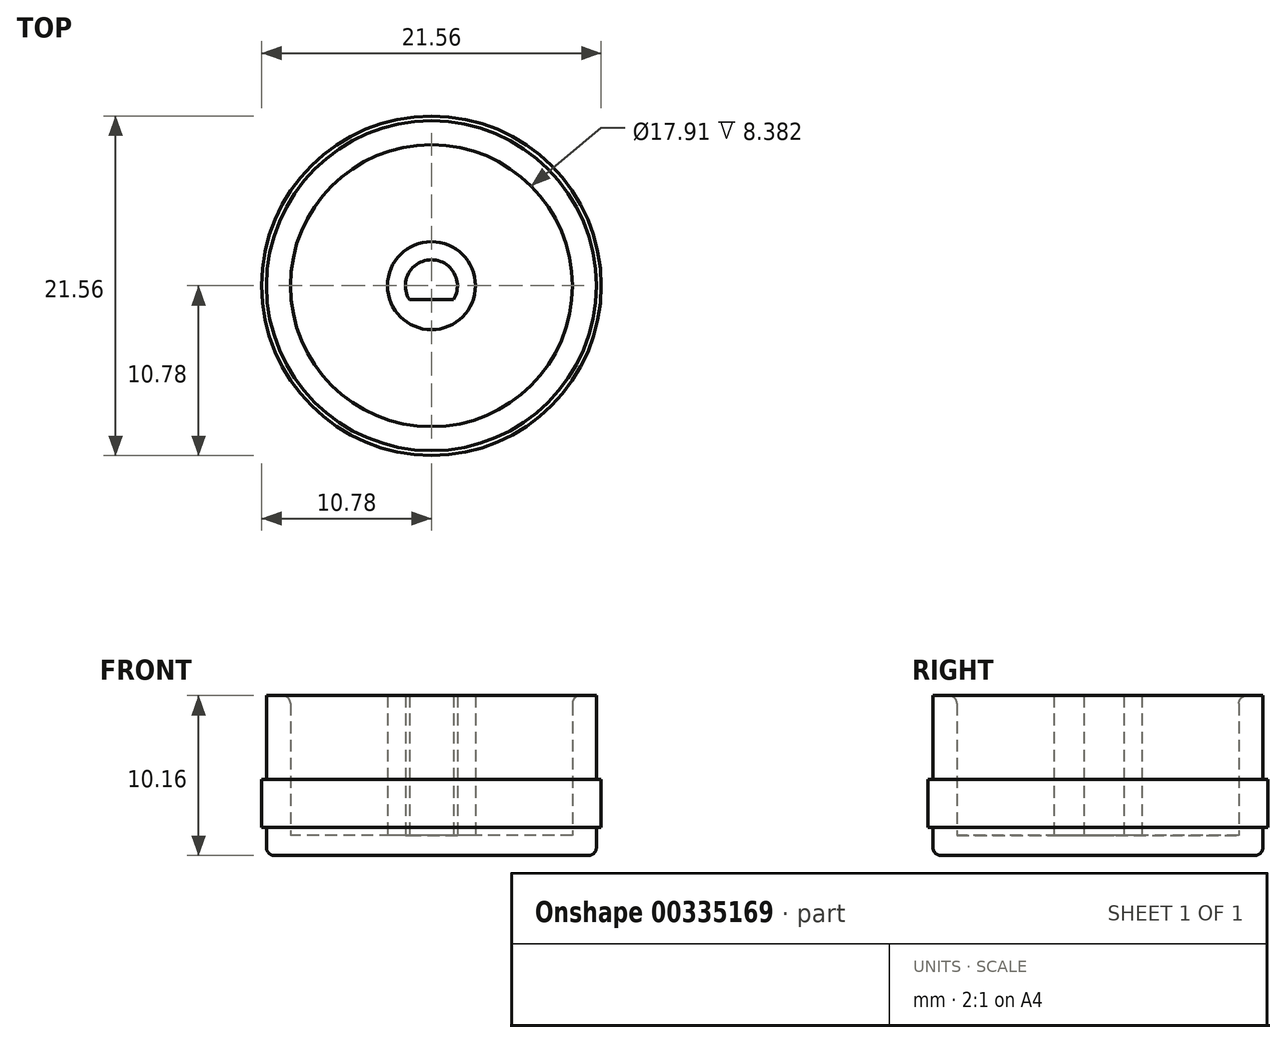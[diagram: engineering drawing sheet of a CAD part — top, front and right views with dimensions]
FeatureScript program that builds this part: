
annotation { "Feature Type Name" : "Feature", "Feature Type Description" : "" }
export const myFeature = defineFeature(function(context is Context, id is Id, definition is map)
    precondition{}
    {
        {
            var Q0;
            Q0=qCreatedBy(makeId("Top.planeOp"),FACE);
            var sketch = newSketch(context, id + "F0", { "sketchPlane" : qUnion([Q0])});
            skCircle(sketch, "E0", {"center": v(0, 0) * mm, "radius": 10.48 * mm});
            skSolve(sketch);
        }
        {
            var Q0;
            Q0=makeQuery(id+"F0.imprint","IMPRINT",FACE,{"disambiguationData":[TD([[makeQuery(id+"F0.imprint","IMPRINT",EDGE,{"derivedFrom":sQuery(id+"F0.wireOp",EDGE,"E0")}),1.0]])]});
            extrude(context, id + "F1", {"entities" : qUnion([Q0]), "depth" : 1.27 * mm});
        }
        {
            var Q0;
            Q0=makeQuery(id+"F1.opExtrude","CAP_FACE",FACE,{"disambiguationData":[OSD([sQuery(id+"F0.wireOp",EDGE,"E0")])],"isStart":false});
            var sketch = newSketch(context, id + "F2", { "sketchPlane" : qUnion([Q0])});
            skCircle(sketch, "E1", {"center": v(0, 0) * mm, "radius": 10.48 * mm});
            skCircle(sketch, "E2", {"center": v(0, 0) * mm, "radius": 8.95 * mm});
            skCircle(sketch, "E3", {"center": v(0, 0) * mm, "radius": 2.8 * mm});
            skArc(sketch, "E4", {"start": v(1.4, -0.88) * mm, "mid": v(0, 1.65) * mm, "end": v(-1.4, -0.88) * mm});
            skLineSegment(sketch, "E5", {"start": v(-1.4, -0.88) * mm, "end": v(1.4, -0.88) * mm});
            skSolve(sketch);
        }
        {
            var Q0;
            Q0=makeQuery(id+"F2.imprint","IMPRINT",FACE,{"disambiguationData":[TD([[makeQuery(id+"F2.imprint","IMPRINT",EDGE,{"derivedFrom":sQuery(id+"F2.wireOp",EDGE,"E1")}),1.0]])]});
            var Q1;
            Q1=makeQuery(id+"F2.imprint","IMPRINT",FACE,{"disambiguationData":[TD([[makeQuery(id+"F2.imprint","IMPRINT",EDGE,{"derivedFrom":sQuery(id+"F2.wireOp",EDGE,"E3")}),1.0]])]});
            extrude(context, id + "F3", {"entities" : qUnion([Q0, Q1]), "operationType" : NewBodyOperationType.ADD, "depth" : 8.9 * mm});
        }
        {
            var Q0;
            Q0=qCreatedBy(makeId("Right.planeOp"),FACE);
            var sketch = newSketch(context, id + "F4", { "sketchPlane" : qUnion([Q0])});
            skLineSegment(sketch, "E6.bottom", {"start": v(10.48, 4.83) * mm, "end": v(10.78, 4.83) * mm});
            skLineSegment(sketch, "E6.top", {"start": v(10.48, 1.78) * mm, "end": v(10.78, 1.78) * mm});
            skLineSegment(sketch, "E6.left", {"start": v(10.48, 4.83) * mm, "end": v(10.48, 1.78) * mm});
            skLineSegment(sketch, "E6.right", {"start": v(10.78, 4.83) * mm, "end": v(10.78, 1.78) * mm});
            skSolve(sketch);
        }
        {
            var Q0;
            Q0=makeQuery(id+"F4.imprint","IMPRINT",FACE,{"disambiguationData":[TD([[makeQuery(id+"F4.imprint","IMPRINT",EDGE,{"derivedFrom":sQuery(id+"F4.wireOp",EDGE,"E6.bottom")}),-1.0]])]});
            var Q1;
            Q1=makeQuery(id+"F3.boolean.opBoolean","MERGE",FACE,{"derivedFrom":[makeQuery(id+"F1.opExtrude","SWEPT_FACE",FACE,{"disambiguationData":[OSD([sQuery(id+"F0.wireOp",EDGE,"E0")])]}),makeQuery(id+"F3.opExtrude","SWEPT_FACE",FACE,{"disambiguationData":[OSD([sQuery(id+"F2.wireOp",EDGE,"E1")])]})]});
            revolve(context, id + "F5", {"operationType" : NewBodyOperationType.ADD, "entities" : qUnion([Q0]), "axis" : qUnion([Q1]), "revolveType" : RevolveType.FULL});
        }
        {
            var Q0;
            Q0=makeQuery(id+"F1.opExtrude","CAP_EDGE",EDGE,{"disambiguationData":[OSD([sQuery(id+"F0.wireOp",EDGE,"E0")])],"isStart":true});
            var Q1;
            Q1=makeQuery(id+"F3.opExtrude","CAP_EDGE",EDGE,{"disambiguationData":[OSD([sQuery(id+"F2.wireOp",EDGE,"E2")])],"isStart":false});
            fillet(context, id + "F6", {"entities" : qUnion([Q0, Q1]), "radius" : 0.5 * mm, "tangentPropagation" : true, "allowEdgeOverflow" : false});
        }
    });
